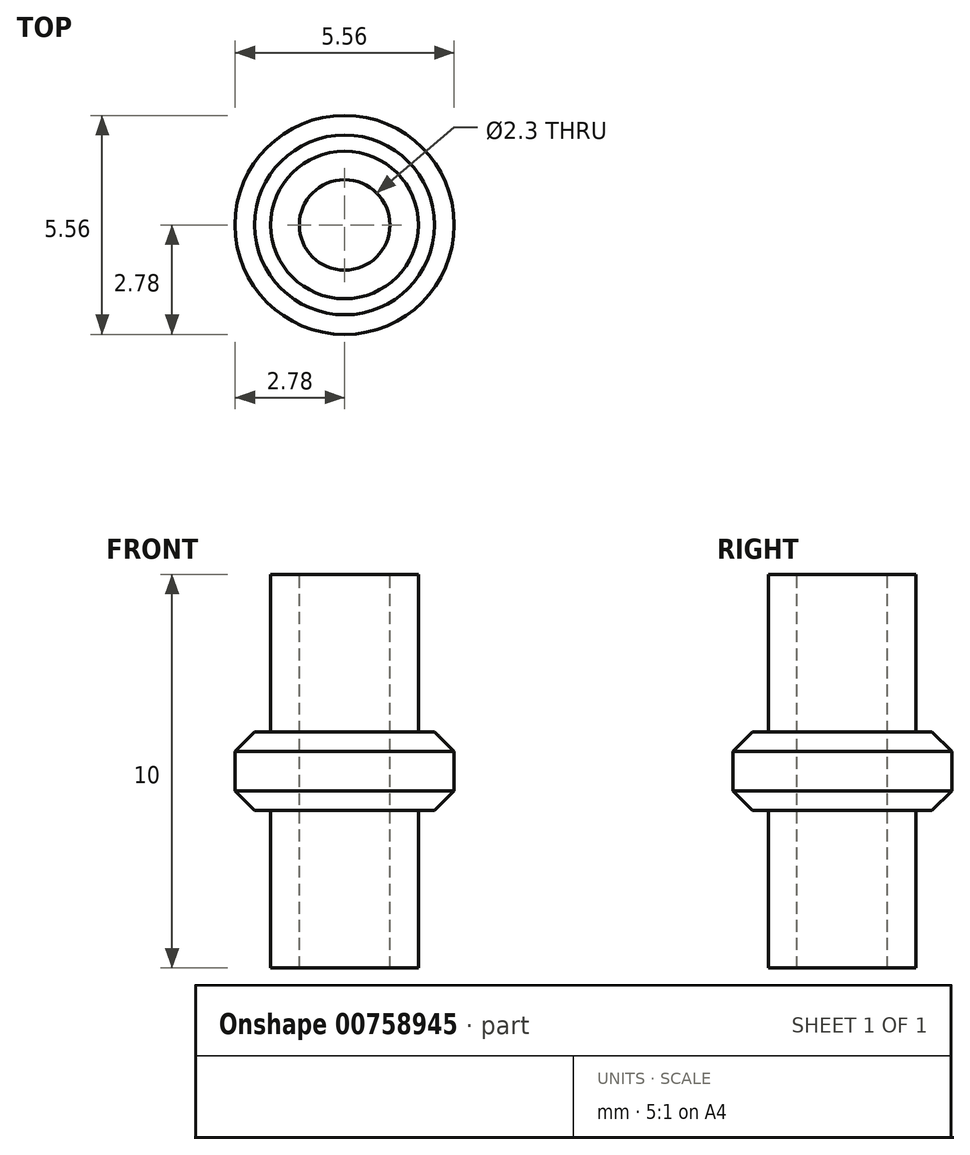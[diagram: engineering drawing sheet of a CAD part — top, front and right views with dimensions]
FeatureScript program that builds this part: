
annotation { "Feature Type Name" : "Feature", "Feature Type Description" : "" }
export const myFeature = defineFeature(function(context is Context, id is Id, definition is map)
    precondition{}
    {
        {
            var Q0;
            Q0=qCreatedBy(makeId("Top.planeOp"),FACE);
            var sketch = newSketch(context, id + "F0", { "sketchPlane" : qUnion([Q0])});
            skCircle(sketch, "E0", {"center": v(0, 0) * mm, "radius": 1.88 * mm});
            skSolve(sketch);
        }
        {
            var Q0;
            Q0=makeQuery(id+"F0.imprint","IMPRINT",FACE,{"disambiguationData":[TD([[makeQuery(id+"F0.imprint","IMPRINT",EDGE,{"derivedFrom":sQuery(id+"F0.wireOp",EDGE,"E0")}),1.0]])]});
            extrude(context, id + "F1", {"entities" : qUnion([Q0]), "depth" : 10 * mm, "offsetDistance" : 25 * mm});
        }
        {
            var Q0;
            Q0=makeQuery(id+"F1.opExtrude","CAP_FACE",FACE,{"disambiguationData":[OSD([sQuery(id+"F0.wireOp",EDGE,"E0")])],"isStart":false});
            var sketch = newSketch(context, id + "F2", { "sketchPlane" : qUnion([Q0])});
            skCircle(sketch, "E1", {"center": v(0, 0) * mm, "radius": 1.15 * mm});
            skSolve(sketch);
        }
        {
            var Q0;
            Q0=makeQuery(id+"F2.imprint","IMPRINT",FACE,{"disambiguationData":[TD([[makeQuery(id+"F2.imprint","IMPRINT",EDGE,{"derivedFrom":sQuery(id+"F2.wireOp",EDGE,"E1")}),1.0]])]});
            extrude(context, id + "F3", {"entities" : qUnion([Q0]), "operationType" : NewBodyOperationType.REMOVE, "oppositeDirection" : true, "depth" : 25 * mm, "offsetDistance" : 25 * mm});
        }
        {
            var Q0;
            Q0=qCreatedBy(makeId("Front.planeOp"),FACE);
            var sketch = newSketch(context, id + "F4", { "sketchPlane" : qUnion([Q0])});
            skLineSegment(sketch, "E2", {"start": v(0, 0) * mm, "end": v(1.78, 0) * mm});
            skLineSegment(sketch, "E3", {"start": v(1.78, 0) * mm, "end": v(1.78, 4) * mm});
            skLineSegment(sketch, "E4", {"start": v(1.78, 4) * mm, "end": v(2.78, 4) * mm});
            skLineSegment(sketch, "E5", {"start": v(2.78, 4) * mm, "end": v(2.78, 6) * mm});
            skLineSegment(sketch, "E6", {"start": v(2.78, 6) * mm, "end": v(1.74, 6) * mm});
            skLineSegment(sketch, "E7", {"start": v(1.74, 6) * mm, "end": v(1.78, 4) * mm});
            skLineSegment(sketch, "E8", {"start": v(0, 0) * mm, "end": v(0, 7.13) * mm});
            skSolve(sketch);
        }
        {
            var Q0;
            Q0 = qSketchRegion(id + "F4", true);
            var Q1;
            Q1=sQuery(id+"F4.wireOp",EDGE,"E8");
            revolve(context, id + "F5", {"operationType" : NewBodyOperationType.ADD, "surfaceOperationType" : NewSurfaceOperationType.NEW, "entities" : qUnion([Q0]), "axis" : qUnion([Q1]), "revolveType" : RevolveType.FULL});
        }
        {
            var Q0;
            Q0=makeQuery(id+"F5.opRevolve","SWEPT_EDGE",EDGE,{"disambiguationData":[OSD([sQuery(id+"F4.wireOp",EDGE,"E4"),sQuery(id+"F4.wireOp",EDGE,"E5")])]});
            var Q1;
            Q1=makeQuery(id+"F5.opRevolve","SWEPT_EDGE",EDGE,{"disambiguationData":[OSD([sQuery(id+"F4.wireOp",EDGE,"E5"),sQuery(id+"F4.wireOp",EDGE,"E6")])]});
            chamfer(context, id + "F6", {"entities" : qUnion([Q0, Q1]), "width" : .5 * mm, "tangentPropagation" : true});
        }
    });
